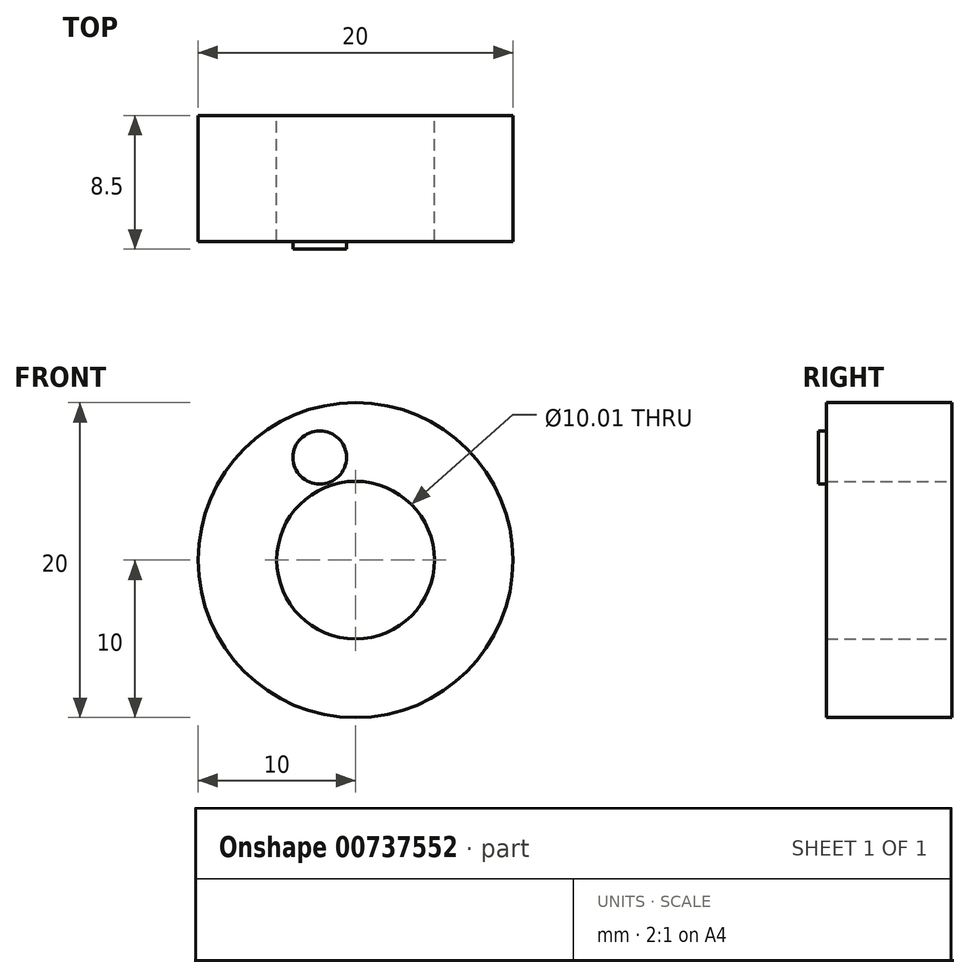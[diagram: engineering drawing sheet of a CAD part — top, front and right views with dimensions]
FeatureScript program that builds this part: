
annotation { "Feature Type Name" : "Feature", "Feature Type Description" : "" }
export const myFeature = defineFeature(function(context is Context, id is Id, definition is map)
    precondition{}
    {
        {
            var Q0;
            Q0=qCreatedBy(makeId("Front.planeOp"),FACE);
            var sketch = newSketch(context, id + "F0", { "sketchPlane" : qUnion([Q0])});
            skCircle(sketch, "E0", {"center": v(0, 0) * mm, "radius": 10 * mm});
            skCircle(sketch, "E1", {"center": v(0, 0) * mm, "radius": 5 * mm});
            skSolve(sketch);
        }
        {
            var Q0;
            Q0=qSketchRegion(id+"F0",true);
            extrude(context, id + "F1", {"entities" : qUnion([Q0]), "depth" : 8 * mm, "offsetDistance" : 25 * mm});
        }
        {
            var Q0;
            Q0=makeQuery(id+"F1.opExtrude","CAP_FACE",FACE,{"disambiguationData":[OSD([sQuery(id+"F0.wireOp",EDGE,"E0"),sQuery(id+"F0.wireOp",EDGE,"E1")])],"isStart":false});
            var sketch = newSketch(context, id + "F2", { "sketchPlane" : qUnion([Q0])});
            skCircle(sketch, "E2", {"center": v(-2.27, 6.52) * mm, "radius": 1.7 * mm});
            skSolve(sketch);
        }
        {
            var Q0;
            Q0 = qSketchRegion(id + "F2", true);
            extrude(context, id + "F3", {"entities" : qUnion([Q0]), "operationType" : NewBodyOperationType.ADD, "depth" : .5 * mm, "offsetDistance" : 25 * mm});
        }
    });
